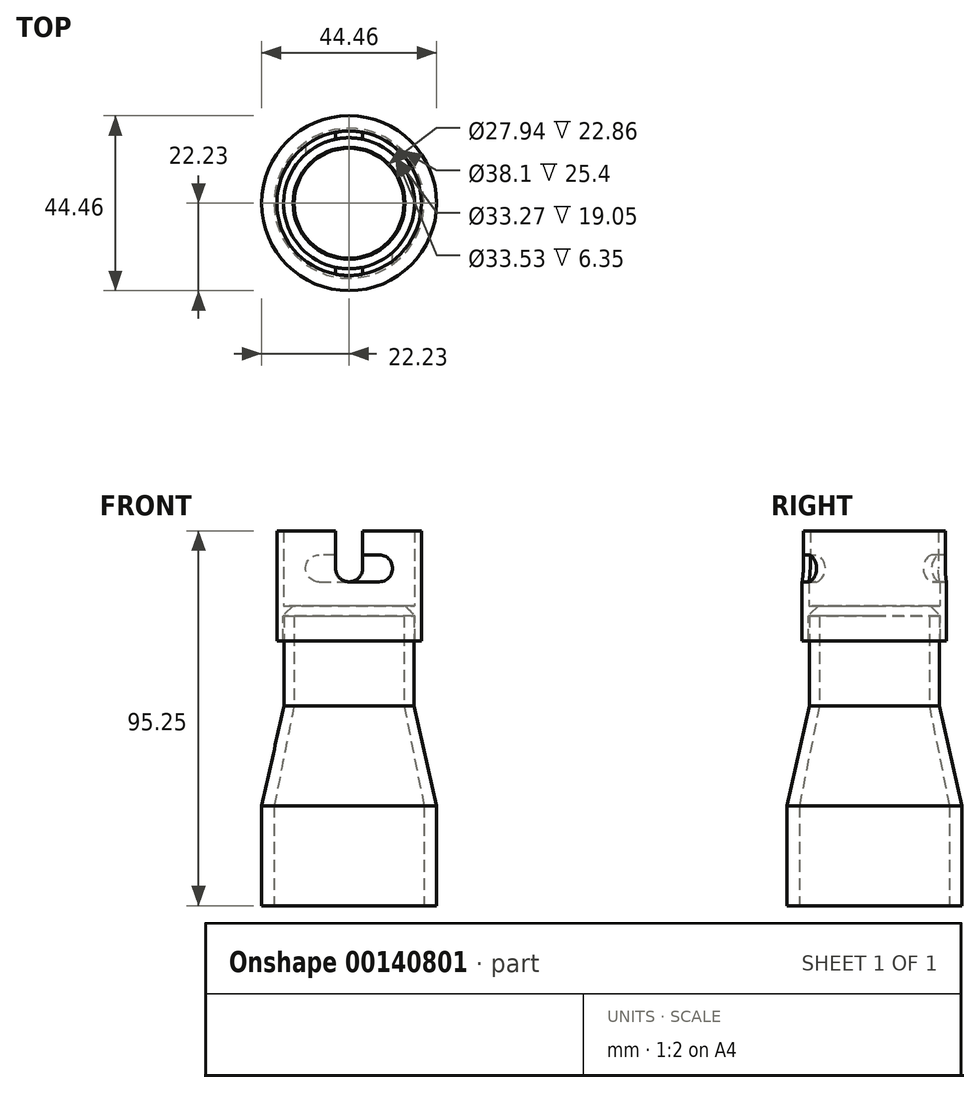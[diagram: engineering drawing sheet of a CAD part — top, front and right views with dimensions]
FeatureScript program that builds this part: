
annotation { "Feature Type Name" : "Feature", "Feature Type Description" : "" }
export const myFeature = defineFeature(function(context is Context, id is Id, definition is map)
    precondition{}
    {
        {
            var Q0;
            Q0=qCreatedBy(makeId("Front.planeOp"),FACE);
            var sketch = newSketch(context, id + "F0", { "sketchPlane" : qUnion([Q0])});
            skLineSegment(sketch, "E0", {"start": v(-19.05, 0) * mm, "end": v(19.05, 0) * mm, "construction": true});
            skLineSegment(sketch, "E1", {"start": v(-13.97, 76.2) * mm, "end": v(-13.97, 50.8) * mm});
            skLineSegment(sketch, "E2", {"start": v(-13.97, 50.8) * mm, "end": v(-19.05, 25.4) * mm});
            skLineSegment(sketch, "E3", {"start": v(-19.05, 25.4) * mm, "end": v(-19.05, 0) * mm});
            skLineSegment(sketch, "E4", {"start": v(-13.97, 76.2) * mm, "end": v(13.97, 76.2) * mm, "construction": true});
            skLineSegment(sketch, "E5", {"start": v(0, 0) * mm, "end": v(0, 76.2) * mm, "construction": true});
            skLineSegment(sketch, "E6", {"start": v(-13.97, 76.2) * mm, "end": v(-16.51, 76.2) * mm});
            skLineSegment(sketch, "E7", {"start": v(-16.51, 76.2) * mm, "end": v(-16.51, 50.8) * mm});
            skLineSegment(sketch, "E8", {"start": v(-19.05, 0) * mm, "end": v(-22.22, 0) * mm});
            skLineSegment(sketch, "E9", {"start": v(-22.22, 0) * mm, "end": v(-22.22, 25.4) * mm});
            skLineSegment(sketch, "E10", {"start": v(-22.22, 25.4) * mm, "end": v(-19.05, 25.4) * mm, "construction": true});
            skLineSegment(sketch, "E11", {"start": v(-16.51, 50.8) * mm, "end": v(-13.97, 50.8) * mm, "construction": true});
            skLineSegment(sketch, "E12", {"start": v(-22.22, 25.4) * mm, "end": v(-16.51, 50.8) * mm});
            skSolve(sketch);
        }
        {
            var Q0;
            Q0=makeQuery(id+"F0.imprint","IMPRINT",FACE,{"disambiguationData":[TD([[makeQuery(id+"F0.imprint","IMPRINT",EDGE,{"derivedFrom":sQuery(id+"F0.wireOp",EDGE,"E1")}),-1.0]])]});
            var Q1;
            Q1=sQuery(id+"F0.wireOp",EDGE,"E5");
            revolve(context, id + "F1", {"entities" : qUnion([Q0]), "axis" : qUnion([Q1]), "revolveType" : RevolveType.FULL});
        }
        {
            var Q0;
            Q0=qCreatedBy(makeId("Front.planeOp"),FACE);
            var sketch = newSketch(context, id + "F2", { "sketchPlane" : qUnion([Q0])});
            skLineSegment(sketch, "E13", {"start": v(0, 0) * mm, "end": v(22.23, 0) * mm, "construction": true});
            skLineSegment(sketch, "E14", {"start": v(22.23, 0) * mm, "end": v(22.23, 3.18) * mm});
            skLineSegment(sketch, "E15", {"start": v(22.23, 3.18) * mm, "end": v(19.05, 0) * mm});
            skLineSegment(sketch, "E16", {"start": v(19.05, 0) * mm, "end": v(22.23, 0) * mm});
            skLineSegment(sketch, "E17", {"start": v(0, 0) * mm, "end": v(0, 76.2) * mm, "construction": true});
            skLineSegment(sketch, "E18", {"start": v(0, 76.2) * mm, "end": v(16.51, 76.2) * mm, "construction": true});
            skLineSegment(sketch, "E19", {"start": v(16.51, 76.2) * mm, "end": v(16.51, 73.66) * mm});
            skLineSegment(sketch, "E20", {"start": v(16.51, 73.66) * mm, "end": v(13.97, 76.2) * mm});
            skLineSegment(sketch, "E21", {"start": v(13.97, 76.2) * mm, "end": v(16.51, 76.2) * mm});
            skSolve(sketch);
        }
        {
            var Q0;
            Q0=makeQuery(id+"F2.imprint","IMPRINT",FACE,{"disambiguationData":[TD([[makeQuery(id+"F2.imprint","IMPRINT",EDGE,{"derivedFrom":sQuery(id+"F2.wireOp",EDGE,"E19")}),-1.0]])]});
            var Q1;
            Q1=sQuery(id+"F2.wireOp",EDGE,"E17");
            var Q2;
            Q2=sQuery(id+"F2.wireOp",EDGE,"E17");
            revolve(context, id + "F3", {"operationType" : NewBodyOperationType.REMOVE, "entities" : qUnion([Q0]), "surfaceEntities" : qUnion([Q1]), "axis" : qUnion([Q2]), "revolveType" : RevolveType.FULL, "oppositeDirection" : true});
        }
        {
            var Q0;
            Q0 = qBodyType(qCreatedBy(id + "F7" ,EDGE), BodyType.WIRE);
            var Q1;
            Q1 = qBodyType(qCreatedBy(id + "FbvmPKB2pPI2nQ0_2" ,EDGE), BodyType.WIRE);
            var Q2;
            Q2 = qBodyType(qCreatedBy(id + "F13" ,EDGE), BodyType.WIRE);
            var Q3;
            Q3 = qBodyType(qCreatedBy(id + "F15" ,EDGE), BodyType.WIRE);
            var Q4;
            Q4 = qBodyType(qCreatedBy(id + "F17" ,EDGE), BodyType.WIRE);
            var Q5;
            Q5=qCreatedBy(makeId("Top.planeOp"),FACE);
            cPlane(context, id + "F4", {"entities" : qUnion([Q0, Q1, Q2, Q3, Q4, Q5]), "cplaneType" : CPlaneType.OFFSET, "offset" : 76.2 * mm, "width" : 152.4 * mm, "height" : 152.4 * mm});
        }
        {
            var Q0;
            Q0=qCreatedBy(id+"F4.planeOp",FACE);
            var sketch = newSketch(context, id + "F5", { "sketchPlane" : qUnion([Q0])});
            skCircle(sketch, "E22", {"center": v(0, 0) * mm, "radius": 16.76 * mm});
            skCircle(sketch, "E23", {"center": v(0, 0) * mm, "radius": 18.35 * mm});
            skSolve(sketch);
        }
        {
            var Q0;
            Q0=makeQuery(id+"F5.imprint","IMPRINT",FACE,{"disambiguationData":[TD([[makeQuery(id+"F5.imprint","IMPRINT",EDGE,{"derivedFrom":sQuery(id+"F5.wireOp",EDGE,"E22")}),-1.0]])]});
            var Q1;
            Q1=makeQuery(id+"F5.imprint","IMPRINT",FACE,{"disambiguationData":[TD([[makeQuery(id+"F5.imprint","IMPRINT",EDGE,{"derivedFrom":sQuery(id+"F5.wireOp",EDGE,"Htsypiwg-FF2L-hJYJ-rkWw-JBcisURJMBwS")}),-1.0]])]});
            extrude(context, id + "F6", {"entities" : qUnion([Q0, Q1]), "oppositeDirection" : true, "depth" : 8.9 * mm});
        }
        {
            var Q0;
            Q0=qCreatedBy(id+"F4.planeOp",FACE);
            var sketch = newSketch(context, id + "F7", { "sketchPlane" : qUnion([Q0])});
            skCircle(sketch, "E24", {"center": v(0, 0) * mm, "radius": 13.97 * mm});
            skCircle(sketch, "E25", {"center": v(0, 0) * mm, "radius": 18.35 * mm});
            skSolve(sketch);
        }
        {
            var Q0;
            Q0 = qSketchRegion(id + "F7", true);
            extrude(context, id + "F8", {"entities" : qUnion([Q0]), "operationType" : NewBodyOperationType.ADD, "oppositeDirection" : true, "depth" : 2.54 * mm});
        }
        {
            var Q0;
            Q0=qCreatedBy(makeId("Front.planeOp"),FACE);
            var sketch = newSketch(context, id + "F9", { "sketchPlane" : qUnion([Q0])});
            skLineSegment(sketch, "E26", {"start": v(0, 0) * mm, "end": v(0, 76.2) * mm, "construction": true});
            skLineSegment(sketch, "E27", {"start": v(0, 76.2) * mm, "end": v(16.76, 76.2) * mm, "construction": true});
            skLineSegment(sketch, "E28", {"start": v(16.76, 73.66) * mm, "end": v(14.22, 76.2) * mm});
            skLineSegment(sketch, "E29", {"start": v(14.22, 76.2) * mm, "end": v(16.76, 76.2) * mm});
            skLineSegment(sketch, "E30", {"start": v(16.76, 73.66) * mm, "end": v(14.22, 73.66) * mm});
            skLineSegment(sketch, "E31", {"start": v(14.22, 73.66) * mm, "end": v(14.22, 76.2) * mm});
            skLineSegment(sketch, "E32", {"start": v(16.76, 73.66) * mm, "end": v(16.76, 76.2) * mm, "construction": true});
            skLineSegment(sketch, "E33", {"start": v(14.22, 73.66) * mm, "end": v(13.97, 73.66) * mm});
            skLineSegment(sketch, "E34", {"start": v(13.97, 73.66) * mm, "end": v(13.97, 76.2) * mm});
            skLineSegment(sketch, "E35", {"start": v(13.97, 76.2) * mm, "end": v(14.22, 76.2) * mm});
            skSolve(sketch);
        }
        {
            var Q0;
            Q0 = qSketchRegion(id + "F9", true);
            var Q1;
            Q1=sQuery(id+"F9.wireOp",EDGE,"E26");
            revolve(context, id + "F10", {"operationType" : NewBodyOperationType.REMOVE, "entities" : qUnion([Q0]), "axis" : qUnion([Q1]), "revolveType" : RevolveType.FULL, "oppositeDirection" : true});
        }
        {
            var Q0;
            Q0=makeQuery(id+"F8.boolean.opBoolean","MERGE",FACE,{"derivedFrom":[makeQuery(id+"F6.opExtrude","CAP_FACE",FACE,{"disambiguationData":[OSD([sQuery(id+"F5.wireOp",EDGE,"E22"),sQuery(id+"F5.wireOp",EDGE,"E23")])],"isStart":true}),makeQuery(id+"F8.opExtrude","CAP_FACE",FACE,{"disambiguationData":[OSD([sQuery(id+"F7.wireOp",EDGE,"E24"),sQuery(id+"F7.wireOp",EDGE,"E25")])],"isStart":true})]});
            var sketch = newSketch(context, id + "F11", { "sketchPlane" : qUnion([Q0])});
            skCircle(sketch, "E36", {"center": v(0, 0) * mm, "radius": 16.64 * mm});
            skCircle(sketch, "E37", {"center": v(0, 0) * mm, "radius": 18.35 * mm});
            skSolve(sketch);
        }
        {
            var Q0;
            Q0 = qSketchRegion(id + "F11", true);
            extrude(context, id + "F12", {"entities" : qUnion([Q0]), "operationType" : NewBodyOperationType.ADD, "depth" : 19.05 * mm});
        }
        {
            var Q0;
            Q0=qCreatedBy(makeId("Front.planeOp"),FACE);
            var sketch = newSketch(context, id + "F13", { "sketchPlane" : qUnion([Q0])});
            skLineSegment(sketch, "E38", {"start": v(0, 0) * mm, "end": v(0, 76.2) * mm, "construction": true});
            skLineSegment(sketch, "E39", {"start": v(0, 76.2) * mm, "end": v(0, 95.25) * mm, "construction": true});
            skLineSegment(sketch, "E40", {"start": v(0, 95.25) * mm, "end": v(3.43, 95.25) * mm});
            skLineSegment(sketch, "E41", {"start": v(3.43, 95.25) * mm, "end": v(3.43, 91.44) * mm});
            skLineSegment(sketch, "E42", {"start": v(-3.43, 88.9) * mm, "end": v(-3.43, 95.25) * mm});
            skLineSegment(sketch, "E43", {"start": v(-3.43, 95.25) * mm, "end": v(0, 95.25) * mm});
            skLineSegment(sketch, "E44", {"start": v(0, 88.9) * mm, "end": v(0, 85.72) * mm, "construction": true});
            skCircle(sketch, "E45", {"center": v(0, 85.72) * mm, "radius": 3.43 * mm});
            skLineSegment(sketch, "E46", {"start": v(3.43, 91.44) * mm, "end": v(3.43, 85.72) * mm});
            skLineSegment(sketch, "E47", {"start": v(-3.43, 88.9) * mm, "end": v(-3.43, 85.72) * mm});
            skSolve(sketch);
        }
        {
            var Q0;
            Q0 = qSketchRegion(id + "F13", true);
            extrude(context, id + "F14", {"entities" : qUnion([Q0]), "operationType" : NewBodyOperationType.REMOVE, "oppositeDirection" : true, "depth" : 25.4 * mm, "hasSecondDirection" : true, "secondDirectionOppositeDirection" : false, "secondDirectionDepth" : 25.4 * mm});
        }
        {
            var Q0;
            Q0=qCreatedBy(makeId("Front.planeOp"),FACE);
            var sketch = newSketch(context, id + "F15", { "sketchPlane" : qUnion([Q0])});
            skLineSegment(sketch, "E48", {"start": v(0, 0) * mm, "end": v(0, 85.73) * mm, "construction": true});
            skLineSegment(sketch, "E49", {"start": v(0, 85.73) * mm, "end": v(7.62, 85.73) * mm});
            skCircle(sketch, "E50", {"center": v(7.62, 85.73) * mm, "radius": 3.43 * mm});
            skLineSegment(sketch, "E51", {"start": v(7.62, 85.73) * mm, "end": v(7.62, 82.3) * mm, "construction": true});
            skLineSegment(sketch, "E52", {"start": v(7.62, 82.3) * mm, "end": v(0, 82.3) * mm});
            skLineSegment(sketch, "E53", {"start": v(0, 82.3) * mm, "end": v(0, 89.15) * mm});
            skLineSegment(sketch, "E54", {"start": v(0, 89.15) * mm, "end": v(7.62, 89.15) * mm});
            skSolve(sketch);
        }
        {
            var Q0;
            Q0 = qSketchRegion(id + "F15", true);
            extrude(context, id + "F16", {"entities" : qUnion([Q0]), "operationType" : NewBodyOperationType.REMOVE, "depth" : 25.4 * mm});
        }
        {
            var Q0;
            Q0=qCreatedBy(makeId("Front.planeOp"),FACE);
            var sketch = newSketch(context, id + "F17", { "sketchPlane" : qUnion([Q0])});
            skLineSegment(sketch, "E55", {"start": v(0, 0) * mm, "end": v(0, 85.73) * mm, "construction": true});
            skLineSegment(sketch, "E56", {"start": v(0, 85.73) * mm, "end": v(-7.62, 85.73) * mm, "construction": true});
            skCircle(sketch, "E57", {"center": v(-7.62, 85.73) * mm, "radius": 3.43 * mm});
            skLineSegment(sketch, "E58", {"start": v(-7.62, 85.73) * mm, "end": v(-7.62, 82.3) * mm, "construction": true});
            skLineSegment(sketch, "E59", {"start": v(-7.62, 82.3) * mm, "end": v(0, 82.3) * mm});
            skLineSegment(sketch, "E60", {"start": v(0, 82.3) * mm, "end": v(0, 89.15) * mm});
            skLineSegment(sketch, "E61", {"start": v(0, 89.15) * mm, "end": v(-7.62, 89.15) * mm});
            skSolve(sketch);
        }
        {
            var Q0;
            Q0 = qSketchRegion(id + "F17", true);
            extrude(context, id + "F18", {"entities" : qUnion([Q0]), "operationType" : NewBodyOperationType.REMOVE, "oppositeDirection" : true, "depth" : 25.4 * mm});
        }
    });
